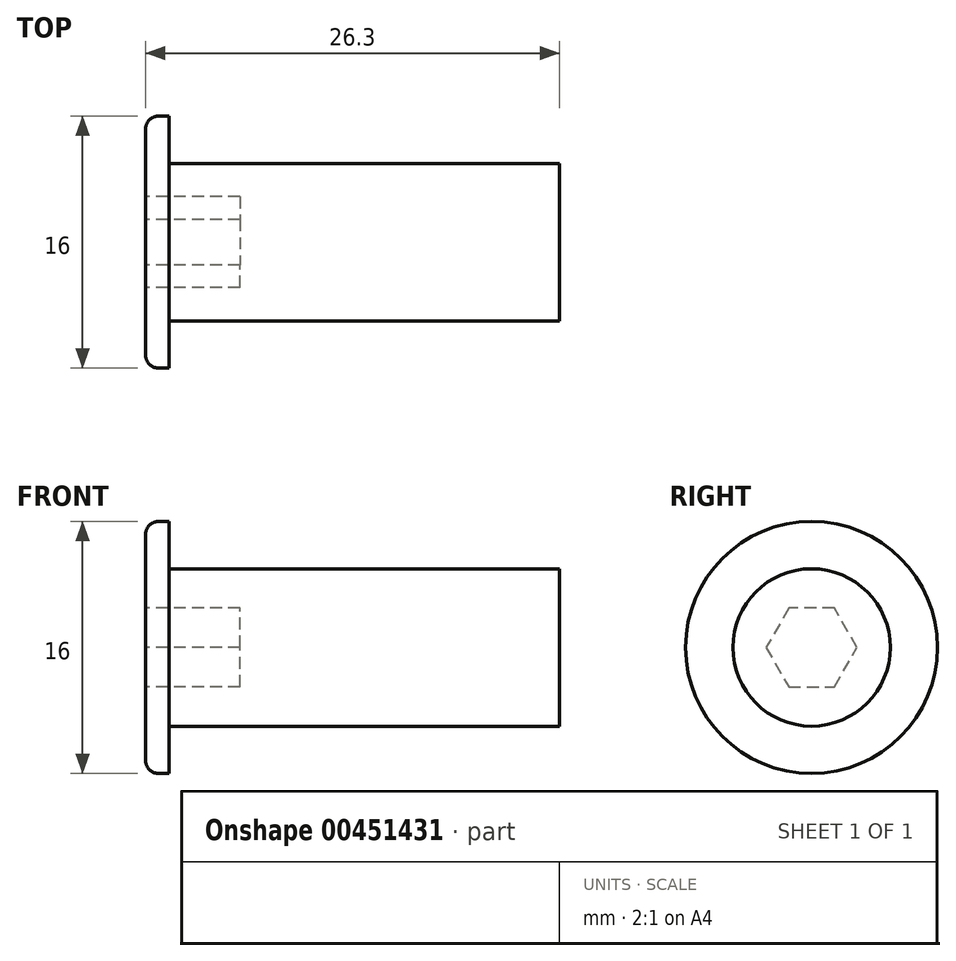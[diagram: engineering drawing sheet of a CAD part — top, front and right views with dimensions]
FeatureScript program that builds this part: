
annotation { "Feature Type Name" : "Feature", "Feature Type Description" : "" }
export const myFeature = defineFeature(function(context is Context, id is Id, definition is map)
    precondition{}
    {
        {
            var Q0;
            Q0=qCreatedBy(makeId("Top.planeOp"),FACE);
            var sketch = newSketch(context, id + "F0", { "sketchPlane" : qUnion([Q0])});
            skLineSegment(sketch, "E0", {"start": v(0, 0) * mm, "end": v(26.3, 0) * mm});
            skLineSegment(sketch, "E1", {"start": v(26.3, 0) * mm, "end": v(26.3, -5) * mm});
            skLineSegment(sketch, "E2", {"start": v(26.3, -5) * mm, "end": v(1.5, -5) * mm});
            skLineSegment(sketch, "E3", {"start": v(1.5, -5) * mm, "end": v(1.5, -8) * mm});
            skLineSegment(sketch, "E4", {"start": v(1.5, -8) * mm, "end": v(0, -8) * mm});
            skLineSegment(sketch, "E5", {"start": v(0, -8) * mm, "end": v(0, 0) * mm});
            skSolve(sketch);
        }
        {
            var Q0;
            Q0=qSketchRegion(id+"F0",true);
            var Q1;
            Q1=sQuery(id+"F0.wireOp",EDGE,"E0");
            revolve(context, id + "F1", {"entities" : qUnion([Q0]), "axis" : qUnion([Q1]), "revolveType" : RevolveType.FULL});
        }
        {
            var Q0;
            Q0=makeQuery(id+"F1.opRevolve","SWEPT_EDGE",EDGE,{"disambiguationData":[OSD([sQuery(id+"F0.wireOp",EDGE,"E4"),sQuery(id+"F0.wireOp",EDGE,"E5")])]});
            fillet(context, id + "F2", {"entities" : qUnion([Q0]), "radius" : 0.8 * mm, "tangentPropagation" : true, "allowEdgeOverflow" : false});
        }
        {
            var Q0;
            Q0=makeQuery(id+"F1.opRevolve","SWEPT_FACE",FACE,{"disambiguationData":[OSD([sQuery(id+"F0.wireOp",EDGE,"E5")])]});
            var sketch = newSketch(context, id + "F3", { "sketchPlane" : qUnion([Q0])});
            skCircle(sketch, "E6.cCircle", {"center": v(0, 0) * mm, "radius": 2.5 * mm, "construction": true});
            skLineSegment(sketch, "E6.0", {"start": v(-1.44, 2.5) * mm, "end": v(1.44, 2.5) * mm});
            skLineSegment(sketch, "E6.1", {"start": v(1.44, 2.5) * mm, "end": v(2.9, 0) * mm});
            skLineSegment(sketch, "E6.2", {"start": v(2.9, 0) * mm, "end": v(1.45, -2.5) * mm});
            skLineSegment(sketch, "E6.3", {"start": v(1.45, -2.5) * mm, "end": v(-1.44, -2.5) * mm});
            skLineSegment(sketch, "E6.4", {"start": v(-1.44, -2.5) * mm, "end": v(-2.89, 0) * mm});
            skLineSegment(sketch, "E6.5", {"start": v(-2.9, 0) * mm, "end": v(-1.44, 2.5) * mm});
            skPoint(sketch, "E6.0.midPoint", {"position": v(0, 2.5) * mm});
            skSolve(sketch);
        }
        {
            var Q0;
            Q0=qSketchRegion(id+"F3",true);
            extrude(context, id + "F4", {"entities" : qUnion([Q0]), "operationType" : NewBodyOperationType.REMOVE, "oppositeDirection" : true, "depth" : 6 * mm});
        }
    });
